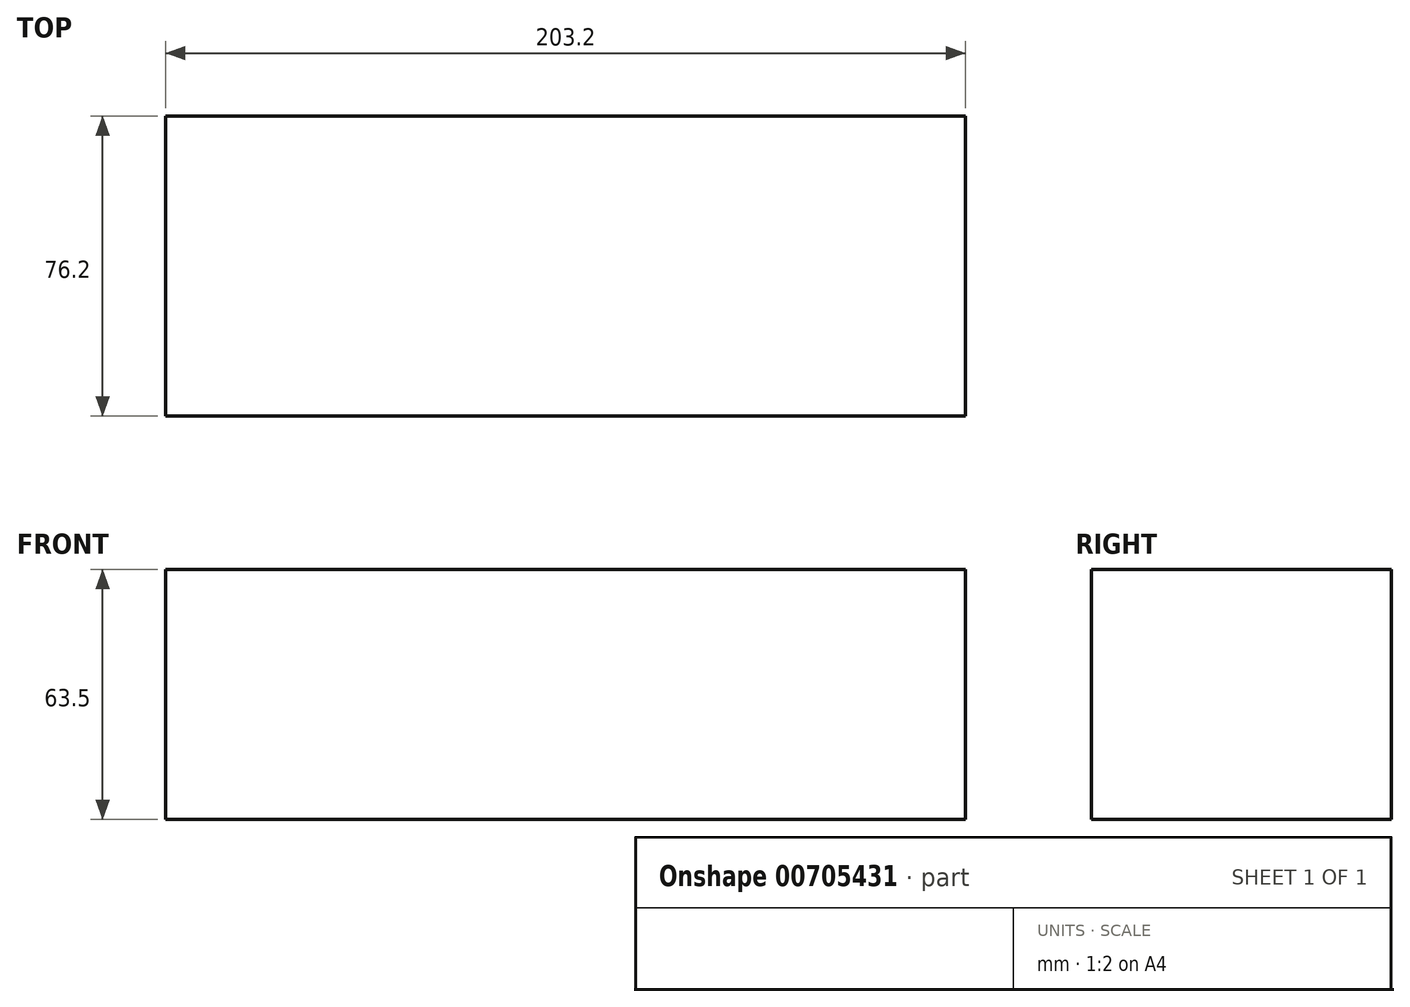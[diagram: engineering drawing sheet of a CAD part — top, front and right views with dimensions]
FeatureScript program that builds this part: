
annotation { "Feature Type Name" : "Feature", "Feature Type Description" : "" }
export const myFeature = defineFeature(function(context is Context, id is Id, definition is map)
    precondition{}
    {
        {
            var Q0;
            Q0=qCreatedBy(makeId("Top.planeOp"),FACE);
            var sketch = newSketch(context, id + "F0", { "sketchPlane" : qUnion([Q0])});
            skLineSegment(sketch, "E0.bottom", {"start": v(101.6, 38.1) * mm, "end": v(-101.6, 38.1) * mm});
            skLineSegment(sketch, "E0.top", {"start": v(101.6, -38.1) * mm, "end": v(-101.6, -38.1) * mm});
            skLineSegment(sketch, "E0.left", {"start": v(101.6, 38.1) * mm, "end": v(101.6, -38.1) * mm});
            skLineSegment(sketch, "E0.right", {"start": v(-101.6, 38.1) * mm, "end": v(-101.6, -38.1) * mm});
            skPoint(sketch, "E0.middle", {"position": v(0, 0) * mm});
            skSolve(sketch);
        }
        {
            var Q0;
            Q0 = qSketchRegion(id + "F0", true);
            extrude(context, id + "F1", {"entities" : qUnion([Q0]), "depth" : 63.5 * mm, "offsetDistance" : 25.4 * mm});
        }
    });
